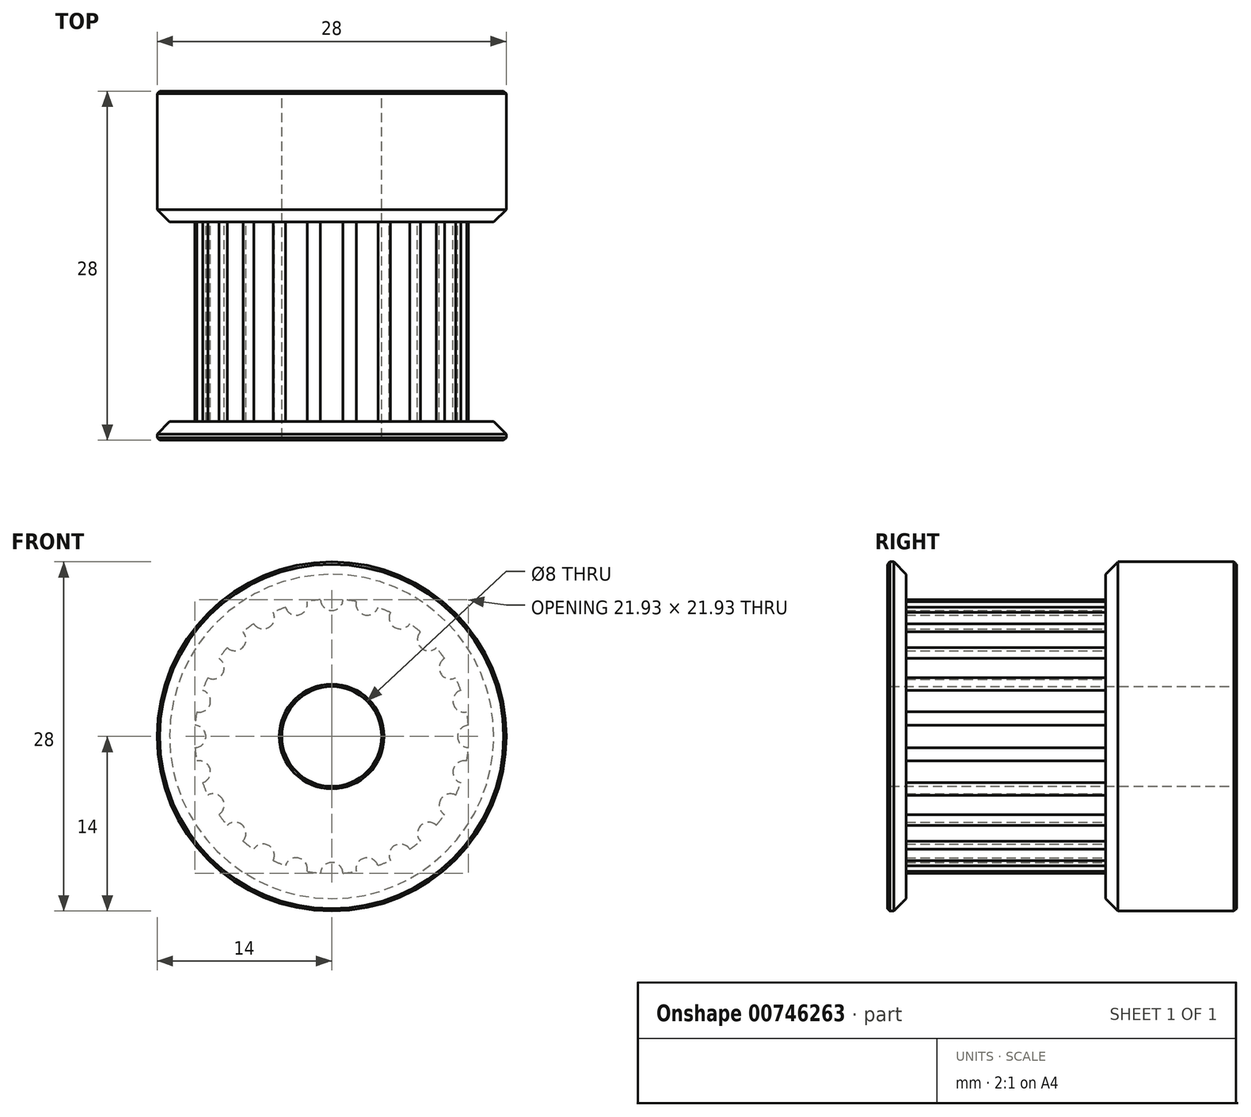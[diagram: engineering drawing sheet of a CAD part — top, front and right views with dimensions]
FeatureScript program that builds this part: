
annotation { "Feature Type Name" : "Feature", "Feature Type Description" : "" }
export const myFeature = defineFeature(function(context is Context, id is Id, definition is map)
    precondition{}
    {
        {
            var Q0;
            Q0=qCreatedBy(makeId("Front.planeOp"),FACE);
            var sketch = newSketch(context, id + "F0", { "sketchPlane" : qUnion([Q0])});
            skCircle(sketch, "E0", {"center": v(0, 0) * mm, "radius": 11 * mm});
            skSolve(sketch);
        }
        {
            var Q0;
            Q0=qSketchRegion(id+"F0",true);
            extrude(context, id + "F1", {"entities" : qUnion([Q0]), "endBound" : BoundingType.SYMMETRIC, "depth" : 16 * mm, "offsetDistance" : 25 * mm});
        }
        {
            var Q0;
            Q0=makeQuery(id+"F1.opExtrude","CAP_FACE",FACE,{"disambiguationData":[OSD([sQuery(id+"F0.wireOp",EDGE,"E0")])],"isStart":false});
            var sketch = newSketch(context, id + "F2", { "sketchPlane" : qUnion([Q0])});
            skCircle(sketch, "E1", {"center": v(0, 0) * mm, "radius": 14 * mm});
            skSolve(sketch);
        }
        {
            var Q0;
            Q0=qSketchRegion(id+"F2",true);
            extrude(context, id + "F3", {"entities" : qUnion([Q0]), "operationType" : NewBodyOperationType.ADD, "depth" : 1.5 * mm, "offsetDistance" : 25 * mm});
        }
        {
            var Q0;
            Q0=makeQuery(id+"F1.opExtrude","CAP_FACE",FACE,{"disambiguationData":[OSD([sQuery(id+"F0.wireOp",EDGE,"E0")])],"isStart":true});
            var sketch = newSketch(context, id + "F4", { "sketchPlane" : qUnion([Q0])});
            skCircle(sketch, "E2", {"center": v(0, 0) * mm, "radius": 14 * mm});
            skSolve(sketch);
        }
        {
            var Q0;
            Q0=qSketchRegion(id+"F4",true);
            extrude(context, id + "F5", {"entities" : qUnion([Q0]), "operationType" : NewBodyOperationType.ADD, "depth" : 10.5 * mm, "offsetDistance" : 25 * mm});
        }
        {
            var Q0;
            Q0=makeQuery(id+"F5.opExtrude","CAP_FACE",FACE,{"disambiguationData":[OSD([sQuery(id+"F4.wireOp",EDGE,"E2")])],"isStart":false});
            var sketch = newSketch(context, id + "F6", { "sketchPlane" : qUnion([Q0])});
            skCircle(sketch, "E3", {"center": v(0, 0) * mm, "radius": 4 * mm});
            skSolve(sketch);
        }
        {
            var Q0;
            Q0=qSketchRegion(id+"F6",true);
            extrude(context, id + "F7", {"entities" : qUnion([Q0]), "operationType" : NewBodyOperationType.REMOVE, "endBound" : BoundingType.THROUGH_ALL, "oppositeDirection" : true, "depth" : 25 * mm, "offsetDistance" : 25 * mm});
        }
        {
            var Q0;
            Q0=makeQuery(id+"F5.opExtrude","CAP_FACE",FACE,{"disambiguationData":[OSD([sQuery(id+"F4.wireOp",EDGE,"E2")])],"isStart":true});
            var sketch = newSketch(context, id + "F8", { "sketchPlane" : qUnion([Q0])});
            skCircle(sketch, "E4", {"center": v(0, 0) * mm, "radius": 8.5 * mm, "construction": true});
            skLineSegment(sketch, "E5", {"start": v(0, 0) * mm, "end": v(0, 11) * mm, "construction": true});
            skCircle(sketch, "E6", {"center": v(0, 11) * mm, "radius": 0.9 * mm});
            skCircle(sketch, "E7.1.0", {"center": v(-2.85, 10.63) * mm, "radius": 0.9 * mm});
            skCircle(sketch, "E7.2.0", {"center": v(-5.5, 9.53) * mm, "radius": 0.9 * mm});
            skCircle(sketch, "E7.3.0", {"center": v(-7.78, 7.78) * mm, "radius": 0.9 * mm});
            skCircle(sketch, "E7.4.0", {"center": v(-9.53, 5.5) * mm, "radius": 0.9 * mm});
            skCircle(sketch, "E7.5.0", {"center": v(-10.63, 2.85) * mm, "radius": 0.9 * mm});
            skCircle(sketch, "E7.6.0", {"center": v(-11, 0) * mm, "radius": 0.9 * mm});
            skCircle(sketch, "E7.7.0", {"center": v(-10.63, -2.85) * mm, "radius": 0.9 * mm});
            skCircle(sketch, "E7.8.0", {"center": v(-9.53, -5.5) * mm, "radius": 0.9 * mm});
            skCircle(sketch, "E7.9.0", {"center": v(-7.78, -7.78) * mm, "radius": 0.9 * mm});
            skCircle(sketch, "E7.10.0", {"center": v(-5.5, -9.53) * mm, "radius": 0.9 * mm});
            skCircle(sketch, "E7.11.0", {"center": v(-2.85, -10.63) * mm, "radius": 0.9 * mm});
            skCircle(sketch, "E7.12.0", {"center": v(0, -11) * mm, "radius": 0.9 * mm});
            skCircle(sketch, "E7.13.0", {"center": v(2.85, -10.63) * mm, "radius": 0.9 * mm});
            skCircle(sketch, "E7.14.0", {"center": v(5.5, -9.53) * mm, "radius": 0.9 * mm});
            skCircle(sketch, "E7.15.0", {"center": v(7.78, -7.78) * mm, "radius": 0.9 * mm});
            skCircle(sketch, "E7.16.0", {"center": v(9.53, -5.5) * mm, "radius": 0.9 * mm});
            skCircle(sketch, "E7.17.0", {"center": v(10.63, -2.85) * mm, "radius": 0.9 * mm});
            skCircle(sketch, "E8.1.18.0", {"center": v(11, 0) * mm, "radius": 0.9 * mm});
            skCircle(sketch, "E8.1.19.0", {"center": v(10.63, 2.85) * mm, "radius": 0.9 * mm});
            skCircle(sketch, "E8.1.20.0", {"center": v(9.53, 5.5) * mm, "radius": 0.9 * mm});
            skCircle(sketch, "E8.1.21.0", {"center": v(7.78, 7.78) * mm, "radius": 0.9 * mm});
            skCircle(sketch, "E8.1.22.0", {"center": v(5.5, 9.53) * mm, "radius": 0.9 * mm});
            skCircle(sketch, "E8.1.23.0", {"center": v(2.85, 10.63) * mm, "radius": 0.9 * mm});
            skSolve(sketch);
        }
        {
            var Q0;
            Q0=qSketchRegion(id+"F8",true);
            var Q1;
            Q1=makeQuery(id+"F3.opExtrude","CAP_FACE",FACE,{"disambiguationData":[OSD([sQuery(id+"F2.wireOp",EDGE,"E1")])],"isStart":true});
            extrude(context, id + "F9", {"entities" : qUnion([Q0]), "operationType" : NewBodyOperationType.REMOVE, "endBound" : BoundingType.UP_TO_SURFACE, "depth" : 25 * mm, "endBoundEntityFace" : qUnion([Q1]), "offsetDistance" : 25 * mm});
        }
        {
            var Q0;
            Q0=makeQuery(id+"F3.opExtrude","CAP_EDGE",EDGE,{"disambiguationData":[OSD([sQuery(id+"F2.wireOp",EDGE,"E1")])],"isStart":true});
            var Q1;
            Q1=makeQuery(id+"F5.opExtrude","CAP_EDGE",EDGE,{"disambiguationData":[OSD([sQuery(id+"F4.wireOp",EDGE,"E2")])],"isStart":true});
            chamfer(context, id + "F10", {"entities" : qUnion([Q0, Q1]), "width" : 1 * mm, "tangentPropagation" : true});
        }
        {
            var Q0;
            Q0=makeQuery(id+"F3.opExtrude","CAP_FACE",FACE,{"disambiguationData":[OSD([sQuery(id+"F2.wireOp",EDGE,"E1")])],"isStart":false});
            var Q1;
            Q1=makeQuery(id+"F5.opExtrude","CAP_FACE",FACE,{"disambiguationData":[OSD([sQuery(id+"F4.wireOp",EDGE,"E2")])],"isStart":false});
            chamfer(context, id + "F11", {"entities" : qUnion([Q0, Q1]), "width" : 0.2 * mm, "tangentPropagation" : true});
        }
    });
